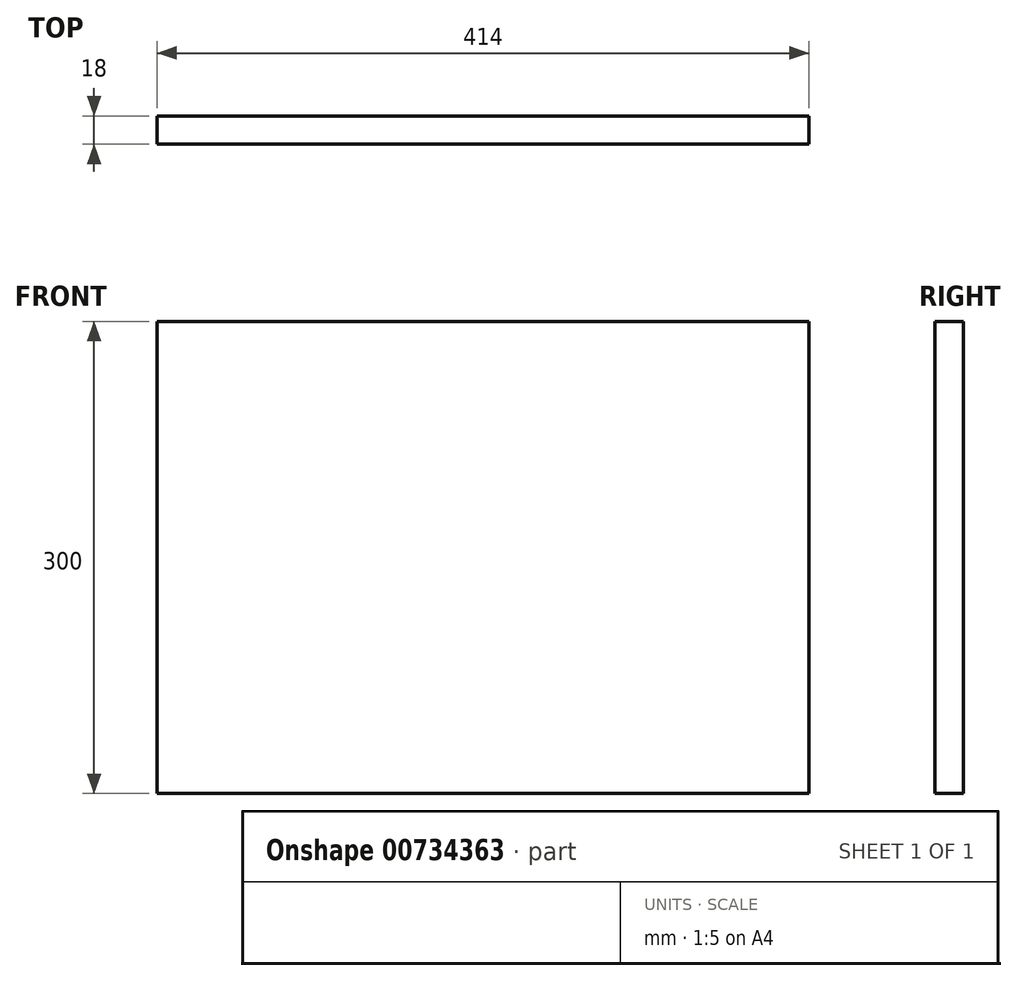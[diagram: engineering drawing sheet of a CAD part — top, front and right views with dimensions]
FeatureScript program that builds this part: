
annotation { "Feature Type Name" : "Feature", "Feature Type Description" : "" }
export const myFeature = defineFeature(function(context is Context, id is Id, definition is map)
    precondition{}
    {
        {
            var Q0;
            Q0=qCreatedBy(makeId("Front.planeOp"),FACE);
            var sketch = newSketch(context, id + "F0", { "sketchPlane" : qUnion([Q0])});
            skLineSegment(sketch, "E0.bottom", {"start": v(-207, -150) * mm, "end": v(207, -150) * mm});
            skLineSegment(sketch, "E0.top", {"start": v(-207, 150) * mm, "end": v(207, 150) * mm});
            skLineSegment(sketch, "E0.left", {"start": v(-207, -150) * mm, "end": v(-207, 150) * mm});
            skLineSegment(sketch, "E0.right", {"start": v(207, -150) * mm, "end": v(207, 150) * mm});
            skPoint(sketch, "E0.middle", {"position": v(0, 0) * mm});
            skSolve(sketch);
        }
        {
            var Q0;
            Q0 = qSketchRegion(id + "F0", true);
            extrude(context, id + "F1", {"entities" : qUnion([Q0]), "depth" : 18 * mm, "offsetDistance" : 25 * mm});
        }
    });
